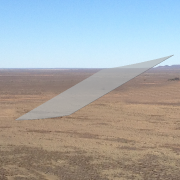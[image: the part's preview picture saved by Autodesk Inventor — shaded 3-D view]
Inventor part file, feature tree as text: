
AUTODESK INVENTOR PART (.ipt)
format: ipt  version: 2013 SP2 (Build 170200200, 200)  size: 150,528 bytes
history: native  units: in
note: dims shown in document units (in); Inventor stores cm internally (conversion verified against a paired STEP export)
features: sketch x3, sweep x1, extrude x1, other x1
ambient origin geometry x8: Origin, YZ Plane, XZ Plane, XY Plane, X Axis, Y Axis, Z Axis, Center Point
feature tree (6):
  sweep  "Sweep2"
  extrude  "Extrusion3"  TaperAngle=0.0deg  [1 undecoded]
  sketch  "Sketch3"  dims[d6=0.0in d7=277.0in d8=90.0in]
  other  "2D Equation Curve2"
  sketch  "Sketch4"  dims[d10=0.25in d11=0.0in]
  sketch  "Sketch8"  dims[d28=2.0in d29=2.0in d32=2.0in d33=300.0in d34=1.1853in d35=201.0in d36=242.0in d37=300.0in d38=0.0in]
note: 1 required parameter value undecoded (feature->parameter linkage not recoverable at this tier; creation-order binding heuristic only, values carry confidence <= 0.55)
